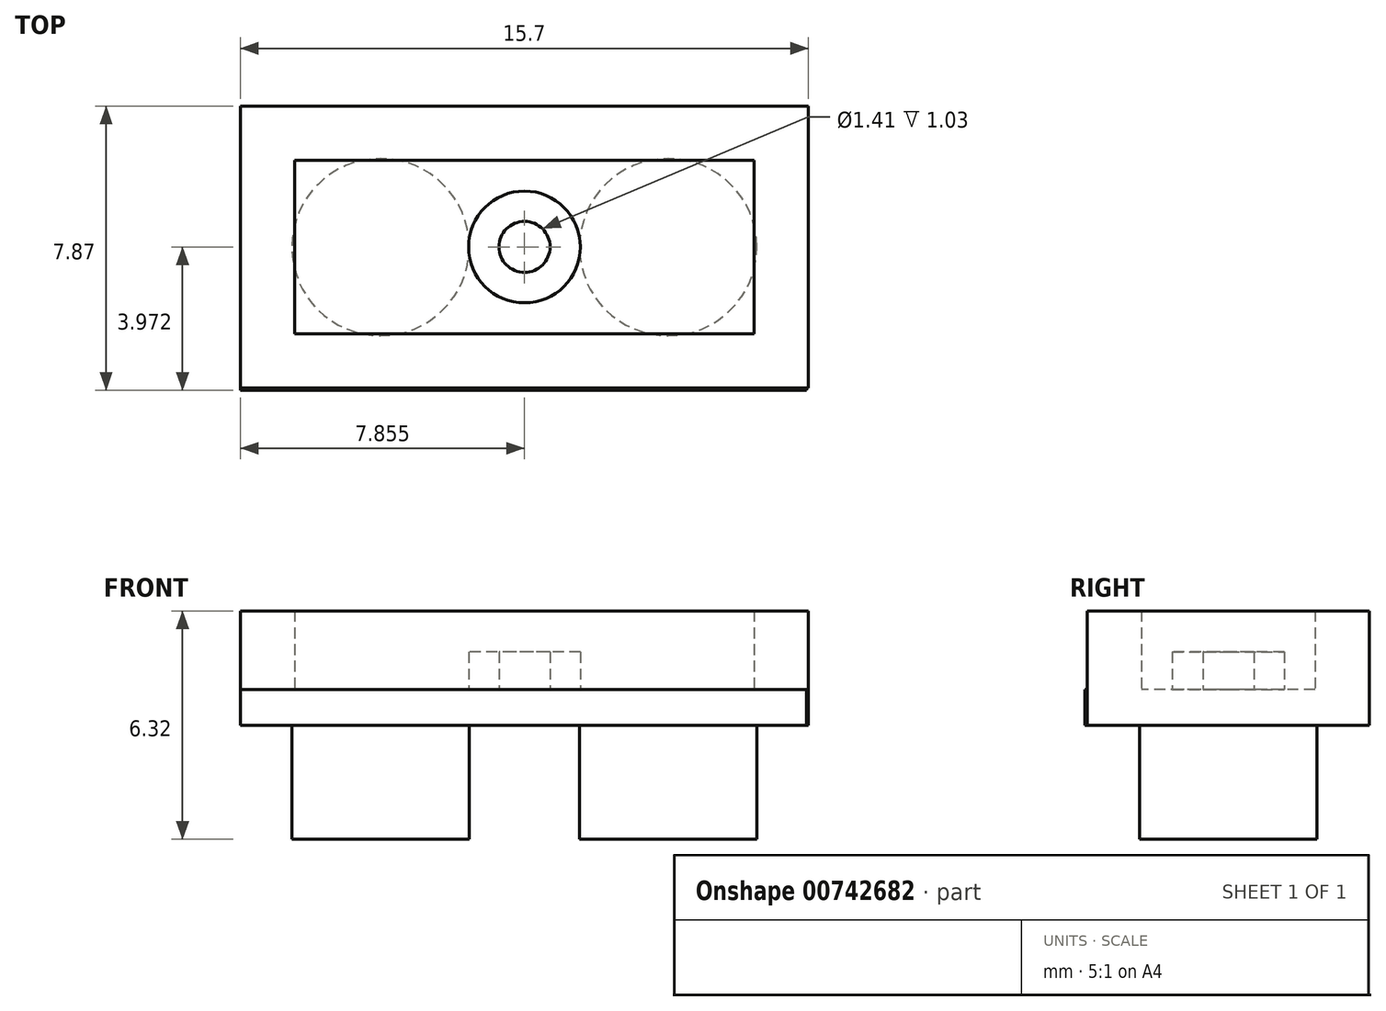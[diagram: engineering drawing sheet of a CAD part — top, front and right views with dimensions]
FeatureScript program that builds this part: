
annotation { "Feature Type Name" : "Feature", "Feature Type Description" : "" }
export const myFeature = defineFeature(function(context is Context, id is Id, definition is map)
    precondition{}
    {
        {
            var Q0;
            Q0=qCreatedBy(makeId("Top.planeOp"),FACE);
            var sketch = newSketch(context, id + "F0", { "sketchPlane" : qUnion([Q0])});
            skLineSegment(sketch, "E0.bottom", {"start": v(-4.63, 3.46) * mm, "end": v(11.07, 3.46) * mm});
            skLineSegment(sketch, "E0.top", {"start": v(-4.63, -4.34) * mm, "end": v(11.07, -4.34) * mm});
            skLineSegment(sketch, "E0.left", {"start": v(-4.63, 3.46) * mm, "end": v(-4.63, -4.34) * mm});
            skLineSegment(sketch, "E0.right", {"start": v(11.07, 3.46) * mm, "end": v(11.07, -4.34) * mm});
            skSolve(sketch);
        }
        {
            var Q0;
            Q0 = qSketchRegion(id + "F0", true);
            extrude(context, id + "F1", {"entities" : qUnion([Q0]), "depth" : 3.17 * mm, "offsetDistance" : 25 * mm});
        }
        {
            var Q0;
            Q0=qCreatedBy(makeId("Top.planeOp"),FACE);
            var sketch = newSketch(context, id + "F2", { "sketchPlane" : qUnion([Q0])});
            skCircle(sketch, "E1", {"center": v(-0.75, -0.44) * mm, "radius": 2.45 * mm});
            skCircle(sketch, "E2", {"center": v(7.2, -0.44) * mm, "radius": 2.45 * mm});
            skSolve(sketch);
        }
        {
            var Q0;
            Q0 = qSketchRegion(id + "F2", true);
            extrude(context, id + "F3", {"entities" : qUnion([Q0]), "operationType" : NewBodyOperationType.ADD, "oppositeDirection" : true, "depth" : 3.15 * mm, "offsetDistance" : 25 * mm});
        }
        {
            var Q0;
            Q0=qCreatedBy(makeId("Top.planeOp"),FACE);
            var sketch = newSketch(context, id + "F4", { "sketchPlane" : qUnion([Q0])});
            skPoint(sketch, "E3.center.orphan", {"position": v(-0.73, -0.44) * mm});
            skPoint(sketch, "E4.center.orphan", {"position": v(7.17, -0.44) * mm});
            skLineSegment(sketch, "E5.bottom", {"start": v(-3.13, 1.96) * mm, "end": v(9.57, 1.96) * mm});
            skLineSegment(sketch, "E5.top", {"start": v(-3.13, -2.84) * mm, "end": v(9.57, -2.84) * mm});
            skLineSegment(sketch, "E5.right", {"start": v(9.57, 1.96) * mm, "end": v(9.57, -2.84) * mm});
            skLineSegment(sketch, "E6", {"start": v(-3.13, 1.96) * mm, "end": v(-3.13, -2.84) * mm});
            skSolve(sketch);
        }
        {
            var Q0;
            Q0 = qSketchRegion(id + "F4", true);
            extrude(context, id + "F5", {"entities" : qUnion([Q0]), "operationType" : NewBodyOperationType.REMOVE, "depth" : 4 * mm, "offsetDistance" : 25 * mm});
        }
        {
            var Q0;
            Q0=qCreatedBy(makeId("Top.planeOp"),FACE);
            var sketch = newSketch(context, id + "F6", { "sketchPlane" : qUnion([Q0])});
            skLineSegment(sketch, "E7.bottom", {"start": v(-4.63, -4.4) * mm, "end": v(11.01, -4.4) * mm});
            skLineSegment(sketch, "E7.top", {"start": v(-4.63, 3.4) * mm, "end": v(11.01, 3.4) * mm});
            skLineSegment(sketch, "E7.left", {"start": v(-4.63, -4.4) * mm, "end": v(-4.63, 3.4) * mm});
            skLineSegment(sketch, "E7.right", {"start": v(11.01, -4.4) * mm, "end": v(11.01, 3.4) * mm});
            skSolve(sketch);
        }
        {
            var Q0;
            Q0 = qSketchRegion(id + "F6", true);
            extrude(context, id + "F7", {"entities" : qUnion([Q0]), "operationType" : NewBodyOperationType.ADD, "depth" : 1 * mm, "offsetDistance" : 25 * mm});
        }
        {
            var Q0;
            Q0=qCreatedBy(makeId("Top.planeOp"),FACE);
            var sketch = newSketch(context, id + "F8", { "sketchPlane" : qUnion([Q0])});
            skCircle(sketch, "E8", {"center": v(3.23, -0.44) * mm, "radius": 1.54 * mm});
            skCircle(sketch, "E9", {"center": v(3.23, -0.44) * mm, "radius": 0.7 * mm});
            skSolve(sketch);
        }
        {
            var Q0;
            Q0 = qSketchRegion(id + "F8", true);
            extrude(context, id + "F9", {"entities" : qUnion([Q0]), "operationType" : NewBodyOperationType.ADD, "depth" : 2.03 * mm, "offsetDistance" : 25 * mm});
        }
    });
